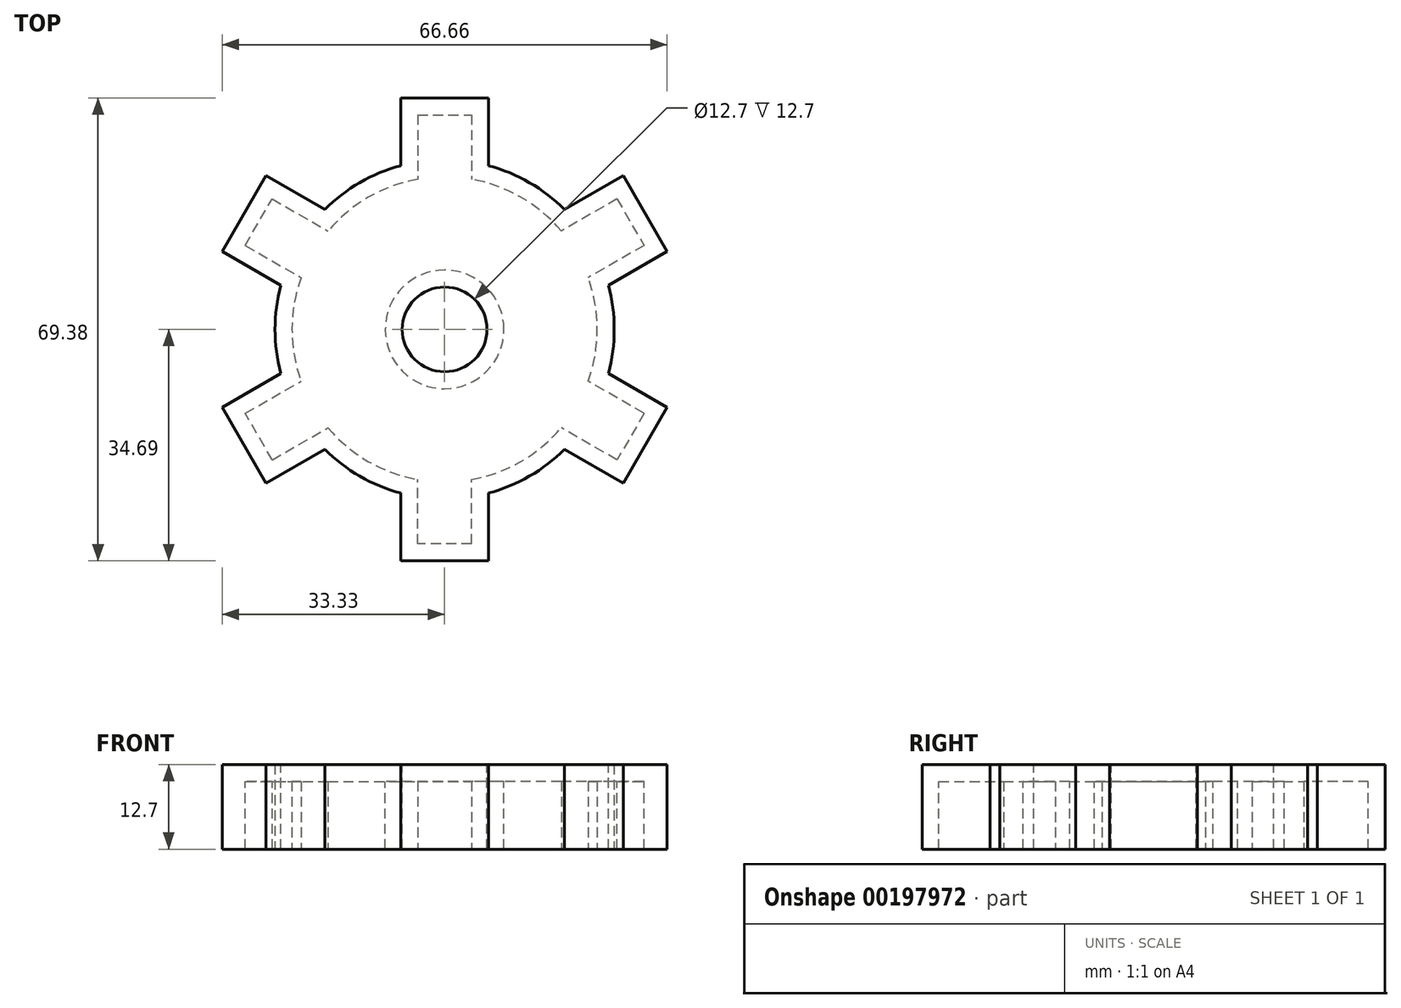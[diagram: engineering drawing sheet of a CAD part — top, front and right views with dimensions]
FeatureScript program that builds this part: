
annotation { "Feature Type Name" : "Feature", "Feature Type Description" : "" }
export const myFeature = defineFeature(function(context is Context, id is Id, definition is map)
    precondition{}
    {
        {
            var Q0;
            Q0=qCreatedBy(makeId("Top.planeOp"),FACE);
            var sketch = newSketch(context, id + "F0", { "sketchPlane" : qUnion([Q0])});
            skCircle(sketch, "E0", {"center": v(0, 0) * mm, "radius": 25.4 * mm});
            skSolve(sketch);
        }
        {
            var Q0;
            Q0=makeQuery(id+"F0.imprint","IMPRINT",FACE,{"disambiguationData":[TD([[makeQuery(id+"F0.imprint","IMPRINT",EDGE,{"derivedFrom":sQuery(id+"F0.wireOp",EDGE,"E0")}),1.0]])]});
            extrude(context, id + "F1", {"entities" : qUnion([Q0]), "depth" : 12.7 * mm});
        }
        {
            var Q0;
            Q0=makeQuery(id+"F1.opExtrude","CAP_FACE",FACE,{"disambiguationData":[OSD([sQuery(id+"F0.wireOp",EDGE,"E0")])],"isStart":false});
            var sketch = newSketch(context, id + "F2", { "sketchPlane" : qUnion([Q0])});
            skLineSegment(sketch, "E1", {"start": v(0, 0) * mm, "end": v(0, 25.4) * mm});
            skLineSegment(sketch, "E2", {"start": v(0, 0) * mm, "end": v(6.57, 24.53) * mm});
            skLineSegment(sketch, "E3", {"start": v(0, 0) * mm, "end": v(-6.57, 24.53) * mm});
            skLineSegment(sketch, "E4", {"start": v(-6.57, 24.53) * mm, "end": v(6.57, 24.53) * mm});
            skLineSegment(sketch, "E5.0", {"start": v(-6.57, 34.7) * mm, "end": v(6.57, 34.7) * mm});
            skLineSegment(sketch, "E6", {"start": v(-6.57, 34.7) * mm, "end": v(-6.57, 24.53) * mm});
            skLineSegment(sketch, "E7", {"start": v(6.57, 34.7) * mm, "end": v(6.57, 24.53) * mm});
            skSolve(sketch);
        }
        {
            var Q0;
            Q0 = qSketchRegion(id + "F2", true);
            extrude(context, id + "F3", {"entities" : qUnion([Q0]), "operationType" : NewBodyOperationType.ADD, "oppositeDirection" : true, "depth" : 12.7 * mm});
        }
        {
            var Q0;
            Q0=qCreatedBy(makeId("Front.planeOp"),FACE);
            var sketch = newSketch(context, id + "F4", { "sketchPlane" : qUnion([Q0])});
            skLineSegment(sketch, "E8", {"start": v(0, 0) * mm, "end": v(0, 55.8) * mm});
            skSolve(sketch);
        }
        {
            var Q0;
            Q0=makeQuery(id+"F1.opExtrude","SWEPT_BODY",BODY,{"disambiguationData":[OSD([sQuery(id+"F0.wireOp",EDGE,"E0")])]});
            var Q1;
            Q1=sQuery(id+"F4.wireOp",EDGE,"E8");
            circularPattern(context, id + "F5", {"operationType" : NewBodyOperationType.ADD, "entities" : qUnion([Q0]), "axis" : qUnion([Q1]), "angle" : 360 * degree, "instanceCount" : 6, "equalSpace" : true});
        }
        {
            var Q0;
            {var subQ0=makeQuery(id+"F3.boolean.opBoolean","MERGE",FACE,{"derivedFrom":[makeQuery(id+"F1.opExtrude","CAP_FACE",FACE,{"disambiguationData":[OSD([sQuery(id+"F0.wireOp",EDGE,"E0")])],"isStart":false}),makeQuery(id+"F3.opExtrude","CAP_FACE",FACE,{"disambiguationData":[OSD([sQuery(id+"F2.wireOp",EDGE,"E2"),sQuery(id+"F2.wireOp",EDGE,"E3"),sQuery(id+"F2.wireOp",EDGE,"E5.0"),sQuery(id+"F2.wireOp",EDGE,"E6"),sQuery(id+"F2.wireOp",EDGE,"E7")])],"isStart":true})]});Q0=makeQuery(id+"F5.boolean.opBoolean","MERGE",FACE,{"derivedFrom":[subQ0,makeQuery(id+"F5.opPattern","COPY",FACE,{"derivedFrom":subQ0,"instanceName":"1"}),makeQuery(id+"F5.opPattern","COPY",FACE,{"derivedFrom":subQ0,"instanceName":"2"}),makeQuery(id+"F5.opPattern","COPY",FACE,{"derivedFrom":subQ0,"instanceName":"3"}),makeQuery(id+"F5.opPattern","COPY",FACE,{"derivedFrom":subQ0,"instanceName":"4"}),makeQuery(id+"F5.opPattern","COPY",FACE,{"derivedFrom":subQ0,"instanceName":"5"})]});}
            var sketch = newSketch(context, id + "F6", { "sketchPlane" : qUnion([Q0])});
            skCircle(sketch, "E9", {"center": v(0, 0) * mm, "radius": 6.35 * mm});
            skSolve(sketch);
        }
        {
            var Q0;
            Q0=makeQuery(id+"F6.imprint","IMPRINT",FACE,{"disambiguationData":[TD([[makeQuery(id+"F6.imprint","IMPRINT",EDGE,{"derivedFrom":sQuery(id+"F6.wireOp",EDGE,"E9")}),1.0]])]});
            extrude(context, id + "F7", {"entities" : qUnion([Q0]), "operationType" : NewBodyOperationType.REMOVE, "oppositeDirection" : true, "depth" : 25.4 * mm});
        }
        {
            var Q0;
            {var subQ0=makeQuery(id+"F3.boolean.opBoolean","MERGE",FACE,{"derivedFrom":[makeQuery(id+"F1.opExtrude","CAP_FACE",FACE,{"disambiguationData":[OSD([sQuery(id+"F0.wireOp",EDGE,"E0")])],"isStart":true}),makeQuery(id+"F3.opExtrude","CAP_FACE",FACE,{"disambiguationData":[OSD([sQuery(id+"F2.wireOp",EDGE,"E2"),sQuery(id+"F2.wireOp",EDGE,"E3"),sQuery(id+"F2.wireOp",EDGE,"E5.0"),sQuery(id+"F2.wireOp",EDGE,"E6"),sQuery(id+"F2.wireOp",EDGE,"E7")])],"isStart":false})]});Q0=makeQuery(id+"F5.boolean.opBoolean","MERGE",FACE,{"derivedFrom":[subQ0,makeQuery(id+"F5.opPattern","COPY",FACE,{"derivedFrom":subQ0,"instanceName":"1"}),makeQuery(id+"F5.opPattern","COPY",FACE,{"derivedFrom":subQ0,"instanceName":"2"}),makeQuery(id+"F5.opPattern","COPY",FACE,{"derivedFrom":subQ0,"instanceName":"3"}),makeQuery(id+"F5.opPattern","COPY",FACE,{"derivedFrom":subQ0,"instanceName":"4"}),makeQuery(id+"F5.opPattern","COPY",FACE,{"derivedFrom":subQ0,"instanceName":"5"})]});}
            shell(context, id + "F8", {"entities" : qUnion([Q0]), "thickness" : 2.54 * mm});
        }
    });
